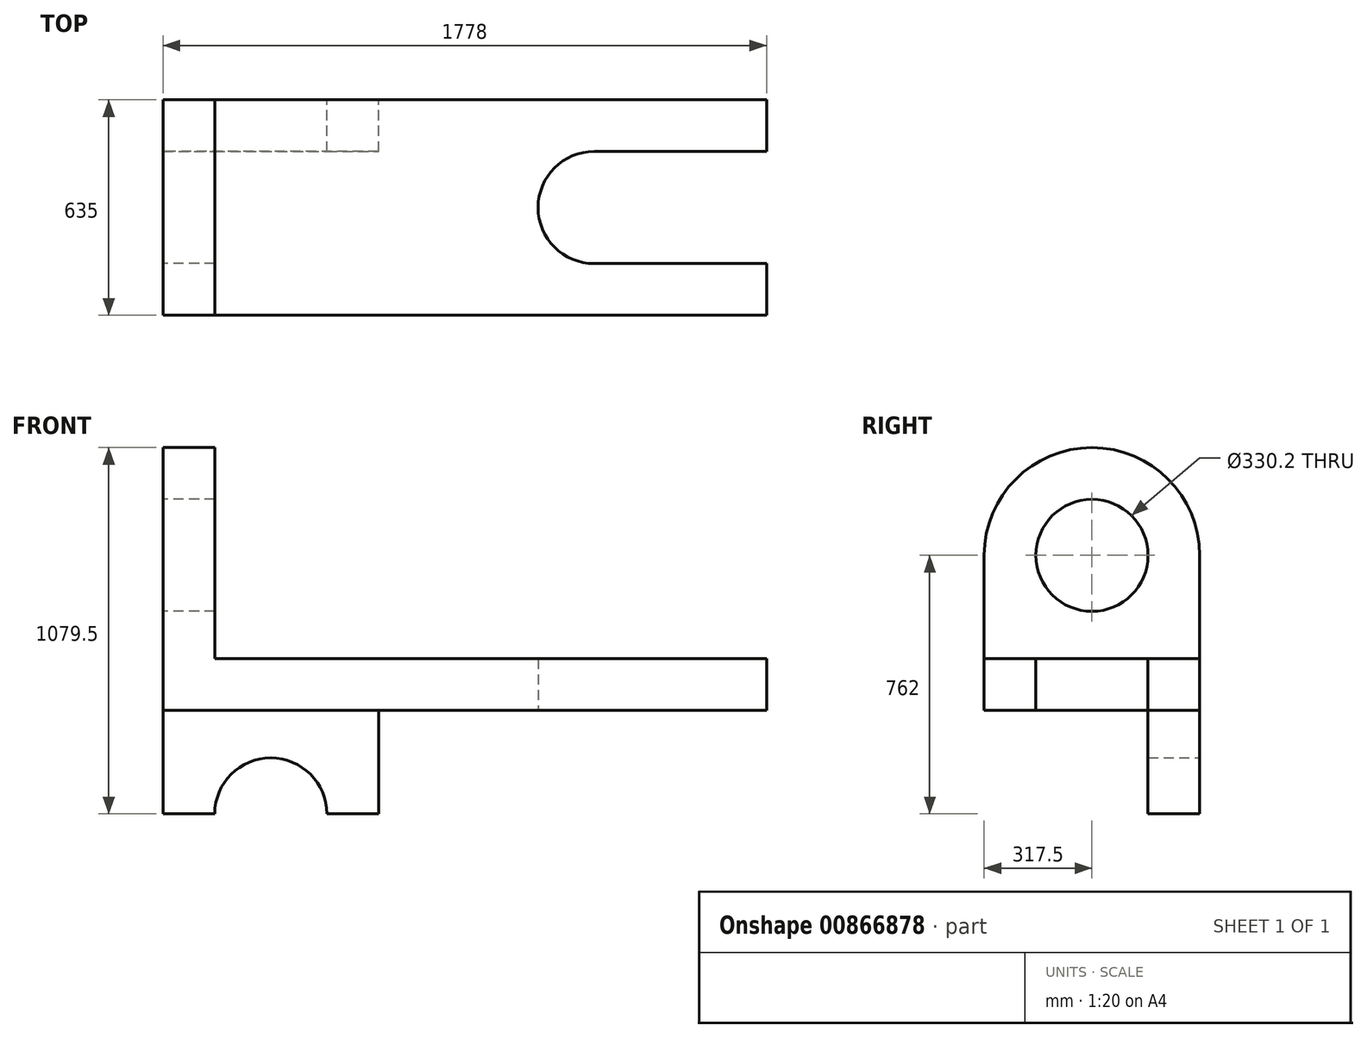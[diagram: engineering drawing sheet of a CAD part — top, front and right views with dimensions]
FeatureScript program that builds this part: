
annotation { "Feature Type Name" : "Feature", "Feature Type Description" : "" }
export const myFeature = defineFeature(function(context is Context, id is Id, definition is map)
    precondition{}
    {
        {
            var Q0;
            Q0=qCreatedBy(makeId("Top.planeOp"),FACE);
            var sketch = newSketch(context, id + "F0", { "sketchPlane" : qUnion([Q0])});
            skLineSegment(sketch, "E0.bottom", {"start": v(889, 317.5) * mm, "end": v(-889, 317.5) * mm});
            skLineSegment(sketch, "E0.top", {"start": v(889, -317.5) * mm, "end": v(-889, -317.5) * mm});
            skLineSegment(sketch, "E0.left", {"start": v(889, 317.5) * mm, "end": v(889, -317.5) * mm});
            skLineSegment(sketch, "E0.right", {"start": v(-889, 317.5) * mm, "end": v(-889, -317.5) * mm});
            skPoint(sketch, "E0.middle", {"position": v(0, 0) * mm});
            skLineSegment(sketch, "E1.bottom", {"start": v(889, 165.1) * mm, "end": v(381, 165.1) * mm});
            skLineSegment(sketch, "E1.top", {"start": v(889, -165.1) * mm, "end": v(381, -165.1) * mm});
            skLineSegment(sketch, "E1.left", {"start": v(889, 165.1) * mm, "end": v(889, -165.1) * mm});
            skLineSegment(sketch, "E1.right", {"start": v(381, 165.1) * mm, "end": v(381, -165.1) * mm});
            skArc(sketch, "E2", {"start": v(381, 165.1) * mm, "mid": v(215.9, 0) * mm, "end": v(381, -165.1) * mm});
            skSolve(sketch);
        }
        {
            var Q0;
            {var subQ1=sQuery(id+"F0.wireOp",EDGE,"E0.bottom");Q0=makeQuery(id+"F0.imprint","IMPRINT",FACE,{"disambiguationData":[TD([[makeQuery(id+"F0.imprint","IMPRINT",EDGE,{"derivedFrom":subQ1}),1.0]])]});}
            extrude(context, id + "F1", {"entities" : qUnion([Q0]), "depth" : 152.4 * mm, "offsetDistance" : 25.4 * mm});
        }
        {
            var Q0;
            Q0=makeQuery(id+"F1.opExtrude","SWEPT_FACE",FACE,{"disambiguationData":[OSD([sQuery(id+"F0.wireOp",EDGE,"E0.right")])]});
            var sketch = newSketch(context, id + "F2", { "sketchPlane" : qUnion([Q0])});
            skLineSegment(sketch, "E3.bottom", {"start": v(-317.5, 0) * mm, "end": v(317.5, 0) * mm});
            skLineSegment(sketch, "E3.top", {"start": v(-317.5, 457.2) * mm, "end": v(317.5, 457.2) * mm});
            skLineSegment(sketch, "E3.left", {"start": v(-317.5, 0) * mm, "end": v(-317.5, 457.2) * mm});
            skLineSegment(sketch, "E3.right", {"start": v(317.5, 0) * mm, "end": v(317.5, 457.2) * mm});
            skArc(sketch, "E4", {"start": v(317.5, 457.2) * mm, "mid": v(0, 774.7) * mm, "end": v(-317.5, 457.2) * mm});
            skCircle(sketch, "E5", {"center": v(0, 457.2) * mm, "radius": 165.1 * mm});
            skSolve(sketch);
        }
        {
            var Q0;
            {var subQ1=makeQuery(id+"F1.opExtrude","CAP_EDGE",EDGE,{"disambiguationData":[OSD([sQuery(id+"F0.wireOp",EDGE,"E0.right")])],"isStart":false});Q0=makeQuery(id+"F2.imprint","IMPRINT",FACE,{"disambiguationData":[TD([[makeQuery(id+"F2.imprint","IMPRINT",EDGE,{"derivedFrom":subQ1}),1.0]])]});}
            var Q1;
            {var subQ0=sQuery(id+"F2.wireOp",EDGE,"E4");Q1=makeQuery(id+"F2.imprint","IMPRINT",FACE,{"disambiguationData":[TD([[makeQuery(id+"F2.imprint","IMPRINT",EDGE,{"derivedFrom":subQ0}),1.0]])]});}
            extrude(context, id + "F3", {"entities" : qUnion([Q0, Q1]), "operationType" : NewBodyOperationType.ADD, "oppositeDirection" : true, "depth" : 152.4 * mm, "offsetDistance" : 25.4 * mm});
        }
        {
            var Q0;
            Q0=makeQuery(id+"F3.boolean.opBoolean","MERGE",FACE,{"derivedFrom":[makeQuery(id+"F1.opExtrude","SWEPT_FACE",FACE,{"disambiguationData":[OSD([sQuery(id+"F0.wireOp",EDGE,"E0.bottom")])]}),makeQuery(id+"F3.opExtrude","SWEPT_FACE",FACE,{"disambiguationData":[OSD([sQuery(id+"F2.wireOp",EDGE,"E3.left")])]})]});
            var sketch = newSketch(context, id + "F4", { "sketchPlane" : qUnion([Q0])});
            skLineSegment(sketch, "E6.bottom", {"start": v(889, 0) * mm, "end": v(254, 0) * mm});
            skLineSegment(sketch, "E6.top", {"start": v(889, -304.8) * mm, "end": v(254, -304.8) * mm});
            skLineSegment(sketch, "E6.left", {"start": v(889, 0) * mm, "end": v(889, -304.8) * mm});
            skLineSegment(sketch, "E6.right", {"start": v(254, 0) * mm, "end": v(254, -304.8) * mm});
            skArc(sketch, "E7", {"start": v(889, -304.8) * mm, "mid": v(571.5, -622.3) * mm, "end": v(254, -304.8) * mm});
            skCircle(sketch, "E8", {"center": v(571.5, -304.8) * mm, "radius": 165.1 * mm});
            skSolve(sketch);
        }
        {
            var Q0;
            Q0=makeQuery(id+"F4.imprint","IMPRINT",FACE,{"disambiguationData":[TD([[makeQuery(id+"F4.imprint","IMPRINT",EDGE,{"derivedFrom":sQuery(id+"F4.wireOp",EDGE,"E6.bottom")}),-1.0]])]});
            var Q1;
            {var subQ0=sQuery(id+"F4.wireOp",EDGE,"E7");Q1=makeQuery(id+"F4.imprint","IMPRINT",FACE,{"disambiguationData":[TD([[makeQuery(id+"F4.imprint","IMPRINT",EDGE,{"derivedFrom":subQ0}),-1.0]])]});}
            extrude(context, id + "F5", {"entities" : qUnion([Q0, Q1]), "operationType" : NewBodyOperationType.ADD, "oppositeDirection" : true, "depth" : 152.4 * mm, "offsetDistance" : 25.4 * mm});
        }
    });
